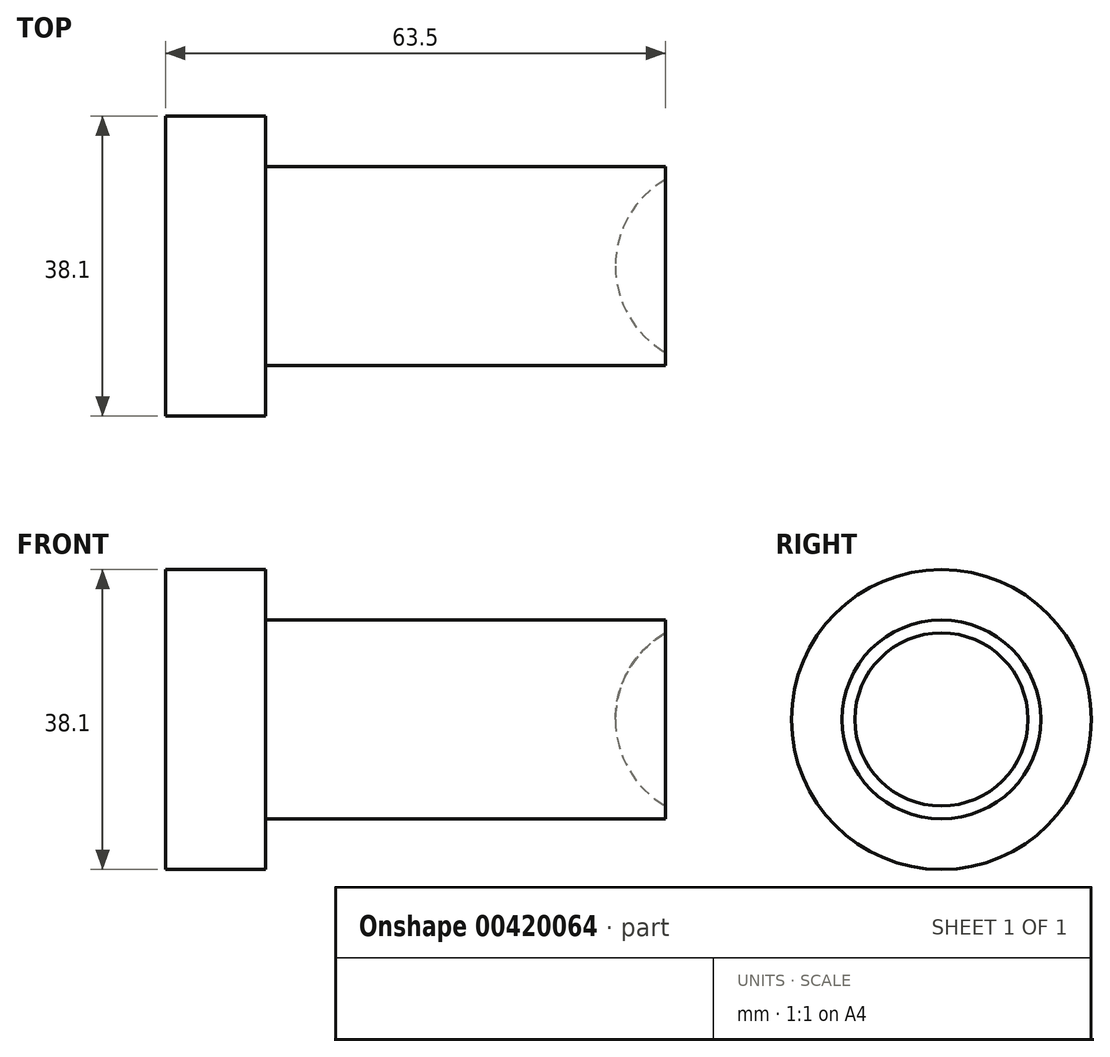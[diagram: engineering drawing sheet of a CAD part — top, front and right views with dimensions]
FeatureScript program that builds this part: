
annotation { "Feature Type Name" : "Feature", "Feature Type Description" : "" }
export const myFeature = defineFeature(function(context is Context, id is Id, definition is map)
    precondition{}
    {
        {
            var Q0;
            Q0=qCreatedBy(makeId("Front.planeOp"),FACE);
            var sketch = newSketch(context, id + "F0", { "sketchPlane" : qUnion([Q0])});
            skLineSegment(sketch, "E0", {"start": v(0, 0) * mm, "end": v(0, 19.05) * mm});
            skLineSegment(sketch, "E1", {"start": v(0, 19.05) * mm, "end": v(12.7, 19.05) * mm});
            skLineSegment(sketch, "E2", {"start": v(12.7, 19.05) * mm, "end": v(12.7, 12.64) * mm});
            skLineSegment(sketch, "E3", {"start": v(12.7, 12.64) * mm, "end": v(63.5, 12.64) * mm});
            skLineSegment(sketch, "E4", {"start": v(63.5, 12.64) * mm, "end": v(63.5, 0) * mm});
            skLineSegment(sketch, "E5", {"start": v(63.5, 0) * mm, "end": v(0, 0) * mm});
            skSolve(sketch);
        }
        {
            var Q0;
            Q0=makeQuery(id+"F0.imprint","IMPRINT",FACE,{"disambiguationData":[TD([[makeQuery(id+"F0.imprint","IMPRINT",EDGE,{"derivedFrom":sQuery(id+"F0.wireOp",EDGE,"E0")}),-1.0]])]});
            var Q1;
            Q1=sQuery(id+"F0.wireOp",EDGE,"E5");
            revolve(context, id + "F1", {"entities" : qUnion([Q0]), "axis" : qUnion([Q1]), "revolveType" : RevolveType.FULL});
        }
        {
            var Q0;
            Q0=qCreatedBy(makeId("Front.planeOp"),FACE);
            var sketch = newSketch(context, id + "F2", { "sketchPlane" : qUnion([Q0])});
            skArc(sketch, "E6", {"start": v(63.5, 11) * mm, "mid": v(58.85, 6.35) * mm, "end": v(57.15, 0) * mm});
            skLineSegment(sketch, "E7", {"start": v(57.15, 0) * mm, "end": v(63.5, 0) * mm});
            skLineSegment(sketch, "E8", {"start": v(63.5, 0) * mm, "end": v(63.5, 11) * mm});
            skSolve(sketch);
        }
        {
            var Q0;
            Q0 = qSketchRegion(id + "F2", true);
            var Q1;
            Q1=sQuery(id+"F2.wireOp",EDGE,"E7");
            revolve(context, id + "F3", {"operationType" : NewBodyOperationType.REMOVE, "entities" : qUnion([Q0]), "axis" : qUnion([Q1]), "revolveType" : RevolveType.FULL, "oppositeDirection" : true});
        }
    });
